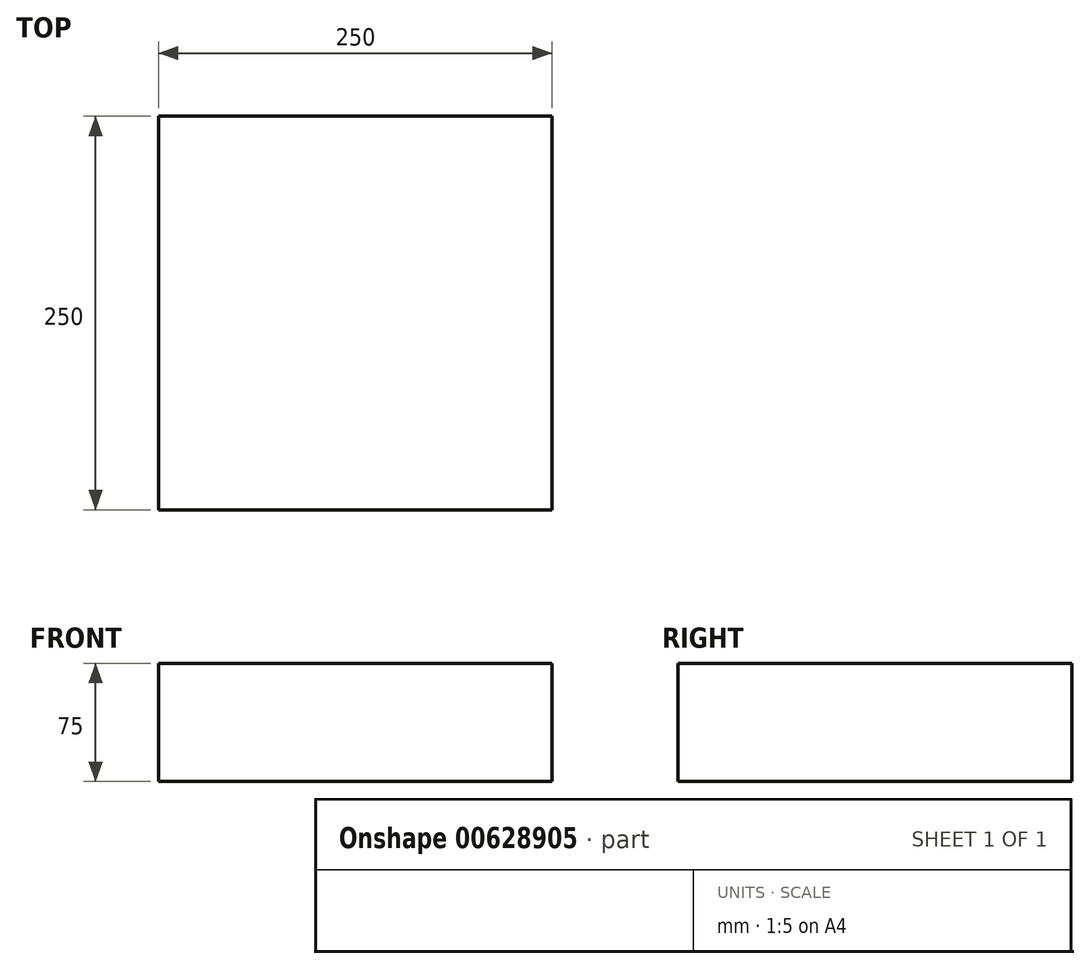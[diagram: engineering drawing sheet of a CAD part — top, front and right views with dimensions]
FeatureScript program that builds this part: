
annotation { "Feature Type Name" : "Feature", "Feature Type Description" : "" }
export const myFeature = defineFeature(function(context is Context, id is Id, definition is map)
    precondition{}
    {
        {
            var Q0;
            Q0=qCreatedBy(makeId("Top.planeOp"),FACE);
            var sketch = newSketch(context, id + "F0", { "sketchPlane" : qUnion([Q0])});
            skPoint(sketch, "E0.middle", {"position": v(0, 0) * mm});
            skLineSegment(sketch, "E1.bottom", {"start": v(125, -125) * mm, "end": v(-125, -125) * mm});
            skLineSegment(sketch, "E1.top", {"start": v(125, 125) * mm, "end": v(-125, 125) * mm});
            skLineSegment(sketch, "E1.left", {"start": v(125, -125) * mm, "end": v(125, 125) * mm});
            skLineSegment(sketch, "E1.right", {"start": v(-125, -125) * mm, "end": v(-125, 125) * mm});
            skSolve(sketch);
        }
        {
            var Q0;
            Q0=makeQuery(id+"F0.imprint","IMPRINT",FACE,{"disambiguationData":[TD([[makeQuery(id+"F0.imprint","IMPRINT",EDGE,{"derivedFrom":sQuery(id+"F0.wireOp",EDGE,"E1.bottom")}),-1.0]])]});
            extrude(context, id + "F1", {"entities" : qUnion([Q0]), "depth" : 5 * mm, "offsetDistance" : 25 * mm});
        }
        {
            var Q0;
            Q0=makeQuery(id+"F1.opExtrude","CAP_FACE",FACE,{"disambiguationData":[OSD([sQuery(id+"F0.wireOp",EDGE,"E1.bottom"),sQuery(id+"F0.wireOp",EDGE,"E1.top"),sQuery(id+"F0.wireOp",EDGE,"E1.left"),sQuery(id+"F0.wireOp",EDGE,"E1.right")])],"isStart":false});
            var sketch = newSketch(context, id + "F2", { "sketchPlane" : qUnion([Q0])});
            skLineSegment(sketch, "E2", {"start": v(-105, 115) * mm, "end": v(-105, -125) * mm});
            skLineSegment(sketch, "E3", {"start": v(-105, 115) * mm, "end": v(105, 115) * mm});
            skLineSegment(sketch, "E4", {"start": v(105, 115) * mm, "end": v(105, -125) * mm});
            skLineSegment(sketch, "E5", {"start": v(-105, -125) * mm, "end": v(-125, -125) * mm});
            skLineSegment(sketch, "E6", {"start": v(-125, -125) * mm, "end": v(-125, 125) * mm});
            skLineSegment(sketch, "E7", {"start": v(-125, 125) * mm, "end": v(125, 125) * mm});
            skLineSegment(sketch, "E8", {"start": v(125, 125) * mm, "end": v(125, -125) * mm});
            skLineSegment(sketch, "E9", {"start": v(125, -125) * mm, "end": v(105, -125) * mm});
            skSolve(sketch);
        }
        {
            var Q0;
            Q0=makeQuery(id+"F2.imprint","IMPRINT",FACE,{"disambiguationData":[TD([[makeQuery(id+"F2.imprint","IMPRINT",EDGE,{"derivedFrom":sQuery(id+"F2.wireOp",EDGE,"E2")}),-1.0]])]});
            extrude(context, id + "F3", {"entities" : qUnion([Q0]), "operationType" : NewBodyOperationType.ADD, "depth" : 70 * mm, "offsetDistance" : 25 * mm});
        }
        {
            var Q0;
            Q0=makeQuery(id+"F1.opExtrude","CAP_FACE",FACE,{"disambiguationData":[OSD([sQuery(id+"F0.wireOp",EDGE,"E1.bottom"),sQuery(id+"F0.wireOp",EDGE,"E1.top"),sQuery(id+"F0.wireOp",EDGE,"E1.left"),sQuery(id+"F0.wireOp",EDGE,"E1.right")])],"isStart":false});
            extrude(context, id + "F4", {"entities" : qUnion([Q0]), "operationType" : NewBodyOperationType.ADD, "depth" : 30 * mm, "offsetDistance" : 25 * mm});
        }
        {
            var Q0;
            Q0=makeQuery(id+"F4.opExtrude","CAP_FACE",FACE,{"disambiguationData":[OSD([sQuery(id+"F0.wireOp",EDGE,"E1.bottom"),sQuery(id+"F0.wireOp",EDGE,"E1.top"),sQuery(id+"F0.wireOp",EDGE,"E1.left"),sQuery(id+"F0.wireOp",EDGE,"E1.right")])],"isStart":false});
            var sketch = newSketch(context, id + "F5", { "sketchPlane" : qUnion([Q0])});
            skLineSegment(sketch, "E10", {"start": v(-105, 115) * mm, "end": v(-105, 85) * mm});
            skLineSegment(sketch, "E11", {"start": v(-105, 85) * mm, "end": v(-75, 85) * mm});
            skLineSegment(sketch, "E12", {"start": v(-75, 85) * mm, "end": v(-75, 115) * mm});
            skLineSegment(sketch, "E13", {"start": v(-75, 115) * mm, "end": v(-105, 115) * mm});
            skLineSegment(sketch, "E14.bottom", {"start": v(-75, 115) * mm, "end": v(-45, 115) * mm});
            skLineSegment(sketch, "E14.top", {"start": v(-75, 85) * mm, "end": v(-45, 85) * mm});
            skLineSegment(sketch, "E14.left", {"start": v(-75, 115) * mm, "end": v(-75, 85) * mm});
            skLineSegment(sketch, "E14.right", {"start": v(-45, 115) * mm, "end": v(-45, 85) * mm});
            skLineSegment(sketch, "E15.bottom", {"start": v(-45, 115) * mm, "end": v(-15, 115) * mm});
            skLineSegment(sketch, "E15.top", {"start": v(-45, 85) * mm, "end": v(-15, 85) * mm});
            skLineSegment(sketch, "E15.right", {"start": v(-15, 115) * mm, "end": v(-15, 85) * mm});
            skLineSegment(sketch, "E16.bottom", {"start": v(-15, 115) * mm, "end": v(15, 115) * mm});
            skLineSegment(sketch, "E16.top", {"start": v(-15, 85) * mm, "end": v(15, 85) * mm});
            skLineSegment(sketch, "E16.right", {"start": v(15, 115) * mm, "end": v(15, 85) * mm});
            skLineSegment(sketch, "E17.bottom", {"start": v(15, 115) * mm, "end": v(45, 115) * mm});
            skLineSegment(sketch, "E17.top", {"start": v(15, 85) * mm, "end": v(45, 85) * mm});
            skLineSegment(sketch, "E17.right", {"start": v(45, 115) * mm, "end": v(45, 85) * mm});
            skLineSegment(sketch, "E18.bottom", {"start": v(45, 115) * mm, "end": v(75, 115) * mm});
            skLineSegment(sketch, "E18.top", {"start": v(45, 85) * mm, "end": v(75, 85) * mm});
            skLineSegment(sketch, "E18.right", {"start": v(75, 115) * mm, "end": v(75, 85) * mm});
            skLineSegment(sketch, "E19.bottom", {"start": v(75, 115) * mm, "end": v(105, 115) * mm});
            skLineSegment(sketch, "E19.top", {"start": v(75, 85) * mm, "end": v(105, 85) * mm});
            skLineSegment(sketch, "E19.right", {"start": v(105, 115) * mm, "end": v(105, 85) * mm});
            skLineSegment(sketch, "E20.top", {"start": v(-105, 55) * mm, "end": v(-75, 55) * mm});
            skLineSegment(sketch, "E20.left", {"start": v(-105, 85) * mm, "end": v(-105, 55) * mm});
            skLineSegment(sketch, "E20.right", {"start": v(-75, 85) * mm, "end": v(-75, 55) * mm});
            skLineSegment(sketch, "E21.top", {"start": v(-105, 25) * mm, "end": v(-75, 25) * mm});
            skLineSegment(sketch, "E21.left", {"start": v(-105, 55) * mm, "end": v(-105, 25) * mm});
            skLineSegment(sketch, "E21.right", {"start": v(-75, 55) * mm, "end": v(-75, 25) * mm});
            skLineSegment(sketch, "E22.top", {"start": v(-105, -5) * mm, "end": v(-75, -5) * mm});
            skLineSegment(sketch, "E22.left", {"start": v(-105, 25) * mm, "end": v(-105, -5) * mm});
            skLineSegment(sketch, "E22.right", {"start": v(-75, 25) * mm, "end": v(-75, -5) * mm});
            skLineSegment(sketch, "E23.top", {"start": v(-105, -35) * mm, "end": v(-75, -35) * mm});
            skLineSegment(sketch, "E23.left", {"start": v(-105, -5) * mm, "end": v(-105, -35) * mm});
            skLineSegment(sketch, "E23.right", {"start": v(-75, -5) * mm, "end": v(-75, -35) * mm});
            skLineSegment(sketch, "E24.top", {"start": v(-105, -65) * mm, "end": v(-75, -65) * mm});
            skLineSegment(sketch, "E24.left", {"start": v(-105, -35) * mm, "end": v(-105, -65) * mm});
            skLineSegment(sketch, "E24.right", {"start": v(-75, -35) * mm, "end": v(-75, -65) * mm});
            skLineSegment(sketch, "E25.top", {"start": v(-105, -95) * mm, "end": v(-75, -95) * mm});
            skLineSegment(sketch, "E25.left", {"start": v(-105, -65) * mm, "end": v(-105, -95) * mm});
            skLineSegment(sketch, "E25.right", {"start": v(-75, -65) * mm, "end": v(-75, -95) * mm});
            skLineSegment(sketch, "E26.top", {"start": v(-105, -125) * mm, "end": v(-75, -125) * mm});
            skLineSegment(sketch, "E26.left", {"start": v(-105, -95) * mm, "end": v(-105, -125) * mm});
            skLineSegment(sketch, "E26.right", {"start": v(-75, -95) * mm, "end": v(-75, -125) * mm});
            skLineSegment(sketch, "E27.top", {"start": v(-75, 55) * mm, "end": v(-45, 55) * mm});
            skLineSegment(sketch, "E27.right", {"start": v(-45, 85) * mm, "end": v(-45, 55) * mm});
            skLineSegment(sketch, "E28.top", {"start": v(-45, 55) * mm, "end": v(-15, 55) * mm});
            skLineSegment(sketch, "E28.right", {"start": v(-15, 85) * mm, "end": v(-15, 55) * mm});
            skLineSegment(sketch, "E29.top", {"start": v(-15, 55) * mm, "end": v(15, 55) * mm});
            skLineSegment(sketch, "E29.right", {"start": v(15, 85) * mm, "end": v(15, 55) * mm});
            skLineSegment(sketch, "E30.top", {"start": v(15, 55) * mm, "end": v(45, 55) * mm});
            skLineSegment(sketch, "E30.right", {"start": v(45, 85) * mm, "end": v(45, 55) * mm});
            skLineSegment(sketch, "E31.top", {"start": v(45, 55) * mm, "end": v(75, 55) * mm});
            skLineSegment(sketch, "E31.right", {"start": v(75, 85) * mm, "end": v(75, 55) * mm});
            skLineSegment(sketch, "E32.top", {"start": v(75, 55) * mm, "end": v(105, 55) * mm});
            skLineSegment(sketch, "E32.right", {"start": v(105, 85) * mm, "end": v(105, 55) * mm});
            skLineSegment(sketch, "E33.top", {"start": v(-75, 25) * mm, "end": v(-45, 25) * mm});
            skLineSegment(sketch, "E33.right", {"start": v(-45, 55) * mm, "end": v(-45, 25) * mm});
            skLineSegment(sketch, "E34.top", {"start": v(-45, 25) * mm, "end": v(-15, 25) * mm});
            skLineSegment(sketch, "E34.right", {"start": v(-15, 55) * mm, "end": v(-15, 25) * mm});
            skLineSegment(sketch, "E35.top", {"start": v(-15, 25) * mm, "end": v(15, 25) * mm});
            skLineSegment(sketch, "E35.right", {"start": v(15, 55) * mm, "end": v(15, 25) * mm});
            skLineSegment(sketch, "E36.top", {"start": v(15, 25) * mm, "end": v(45, 25) * mm});
            skLineSegment(sketch, "E36.right", {"start": v(45, 55) * mm, "end": v(45, 25) * mm});
            skLineSegment(sketch, "E37.top", {"start": v(45, 25) * mm, "end": v(75, 25) * mm});
            skLineSegment(sketch, "E37.right", {"start": v(75, 55) * mm, "end": v(75, 25) * mm});
            skPoint(sketch, "E38.oppositeSnap0", {"position": v(105, 70) * mm});
            skLineSegment(sketch, "E38.top", {"start": v(75, 25) * mm, "end": v(105, 25) * mm});
            skLineSegment(sketch, "E38.right", {"start": v(105, 55) * mm, "end": v(105, 25) * mm});
            skLineSegment(sketch, "E39.top", {"start": v(-75, -5) * mm, "end": v(-45, -5) * mm});
            skLineSegment(sketch, "E39.right", {"start": v(-45, 25) * mm, "end": v(-45, -5) * mm});
            skLineSegment(sketch, "E40.top", {"start": v(-45, -5) * mm, "end": v(-15, -5) * mm});
            skLineSegment(sketch, "E40.right", {"start": v(-15, 25) * mm, "end": v(-15, -5) * mm});
            skLineSegment(sketch, "E41.top", {"start": v(-15, -5) * mm, "end": v(15, -5) * mm});
            skLineSegment(sketch, "E41.right", {"start": v(15, 25) * mm, "end": v(15, -5) * mm});
            skLineSegment(sketch, "E42.top", {"start": v(15, -5) * mm, "end": v(45, -5) * mm});
            skLineSegment(sketch, "E42.right", {"start": v(45, 25) * mm, "end": v(45, -5) * mm});
            skLineSegment(sketch, "E43.top", {"start": v(45, -5) * mm, "end": v(75, -5) * mm});
            skLineSegment(sketch, "E43.right", {"start": v(75, 25) * mm, "end": v(75, -5) * mm});
            skLineSegment(sketch, "E44.top", {"start": v(75, -5) * mm, "end": v(105, -5) * mm});
            skLineSegment(sketch, "E44.right", {"start": v(105, 25) * mm, "end": v(105, -5) * mm});
            skLineSegment(sketch, "E45.top", {"start": v(-75, -35) * mm, "end": v(-45, -35) * mm});
            skLineSegment(sketch, "E45.right", {"start": v(-45, -5) * mm, "end": v(-45, -35) * mm});
            skLineSegment(sketch, "E46.top", {"start": v(-45, -35) * mm, "end": v(-15, -35) * mm});
            skLineSegment(sketch, "E46.right", {"start": v(-15, -5) * mm, "end": v(-15, -35) * mm});
            skLineSegment(sketch, "E47.top", {"start": v(-15, -35) * mm, "end": v(15, -35) * mm});
            skLineSegment(sketch, "E47.right", {"start": v(15, -5) * mm, "end": v(15, -35) * mm});
            skLineSegment(sketch, "E48.top", {"start": v(15, -35) * mm, "end": v(45, -35) * mm});
            skLineSegment(sketch, "E48.right", {"start": v(45, -5) * mm, "end": v(45, -35) * mm});
            skLineSegment(sketch, "E49.top", {"start": v(45, -35) * mm, "end": v(75, -35) * mm});
            skLineSegment(sketch, "E49.right", {"start": v(75, -5) * mm, "end": v(75, -35) * mm});
            skLineSegment(sketch, "E50.top", {"start": v(75, -35) * mm, "end": v(105, -35) * mm});
            skLineSegment(sketch, "E50.right", {"start": v(105, -5) * mm, "end": v(105, -35) * mm});
            skLineSegment(sketch, "E51.top", {"start": v(-75, -65) * mm, "end": v(-45, -65) * mm});
            skLineSegment(sketch, "E51.right", {"start": v(-45, -35) * mm, "end": v(-45, -65) * mm});
            skLineSegment(sketch, "E52.top", {"start": v(-75, -95) * mm, "end": v(-45, -95) * mm});
            skLineSegment(sketch, "E52.right", {"start": v(-45, -65) * mm, "end": v(-45, -95) * mm});
            skLineSegment(sketch, "E53.top", {"start": v(-75, -125) * mm, "end": v(-45, -125) * mm});
            skLineSegment(sketch, "E53.right", {"start": v(-45, -95) * mm, "end": v(-45, -125) * mm});
            skPoint(sketch, "E54.oppositeSnap0", {"position": v(-15, 70) * mm});
            skLineSegment(sketch, "E54.top", {"start": v(-45, -65) * mm, "end": v(-15, -65) * mm});
            skLineSegment(sketch, "E54.right", {"start": v(-15, -35) * mm, "end": v(-15, -65) * mm});
            skLineSegment(sketch, "E55.top", {"start": v(-15, -65) * mm, "end": v(15, -65) * mm});
            skLineSegment(sketch, "E55.right", {"start": v(15, -35) * mm, "end": v(15, -65) * mm});
            skLineSegment(sketch, "E56.top", {"start": v(15, -65) * mm, "end": v(45, -65) * mm});
            skLineSegment(sketch, "E56.right", {"start": v(45, -35) * mm, "end": v(45, -65) * mm});
            skLineSegment(sketch, "E57.top", {"start": v(45, -65) * mm, "end": v(75, -65) * mm});
            skLineSegment(sketch, "E57.right", {"start": v(75, -35) * mm, "end": v(75, -65) * mm});
            skLineSegment(sketch, "E58.top", {"start": v(75, -65) * mm, "end": v(105, -65) * mm});
            skLineSegment(sketch, "E58.right", {"start": v(105, -35) * mm, "end": v(105, -65) * mm});
            skLineSegment(sketch, "E59.top", {"start": v(-45, -95) * mm, "end": v(-15, -95) * mm});
            skLineSegment(sketch, "E59.right", {"start": v(-15, -65) * mm, "end": v(-15, -95) * mm});
            skLineSegment(sketch, "E60.top", {"start": v(-15, -95) * mm, "end": v(15, -95) * mm});
            skLineSegment(sketch, "E60.right", {"start": v(15, -65) * mm, "end": v(15, -95) * mm});
            skLineSegment(sketch, "E61.top", {"start": v(-45, -125) * mm, "end": v(-15, -125) * mm});
            skLineSegment(sketch, "E61.right", {"start": v(-15, -95) * mm, "end": v(-15, -125) * mm});
            skLineSegment(sketch, "E62.top", {"start": v(-15, -125) * mm, "end": v(15, -125) * mm});
            skLineSegment(sketch, "E62.right", {"start": v(15, -95) * mm, "end": v(15, -125) * mm});
            skLineSegment(sketch, "E63.top", {"start": v(15, -95) * mm, "end": v(45, -95) * mm});
            skLineSegment(sketch, "E63.right", {"start": v(45, -65) * mm, "end": v(45, -95) * mm});
            skLineSegment(sketch, "E64.top", {"start": v(15, -125) * mm, "end": v(45, -125) * mm});
            skLineSegment(sketch, "E64.right", {"start": v(45, -95) * mm, "end": v(45, -125) * mm});
            skLineSegment(sketch, "E65.top", {"start": v(45, -95) * mm, "end": v(75, -95) * mm});
            skLineSegment(sketch, "E65.right", {"start": v(75, -65) * mm, "end": v(75, -95) * mm});
            skLineSegment(sketch, "E66.top", {"start": v(45, -125) * mm, "end": v(75, -125) * mm});
            skLineSegment(sketch, "E66.right", {"start": v(75, -95) * mm, "end": v(75, -125) * mm});
            skLineSegment(sketch, "E67.top", {"start": v(75, -95) * mm, "end": v(105, -95) * mm});
            skLineSegment(sketch, "E67.right", {"start": v(105, -65) * mm, "end": v(105, -95) * mm});
            skLineSegment(sketch, "E68.top", {"start": v(75, -125) * mm, "end": v(105, -125) * mm});
            skLineSegment(sketch, "E68.right", {"start": v(105, -95) * mm, "end": v(105, -125) * mm});
            skSolve(sketch);
        }
        {
            var Q0;
            Q0=makeQuery(id+"F5.imprint","IMPRINT",FACE,{"disambiguationData":[TD([[makeQuery(id+"F5.imprint","IMPRINT",EDGE,{"derivedFrom":sQuery(id+"F5.wireOp",EDGE,"E10")}),1.0]])]});
            var Q1;
            Q1=makeQuery(id+"F5.imprint","IMPRINT",FACE,{"disambiguationData":[TD([[makeQuery(id+"F5.imprint","IMPRINT",EDGE,{"derivedFrom":sQuery(id+"F5.wireOp",EDGE,"E14.top")}),-1.0]])]});
            var Q2;
            Q2=makeQuery(id+"F5.imprint","IMPRINT",FACE,{"disambiguationData":[TD([[makeQuery(id+"F5.imprint","IMPRINT",EDGE,{"derivedFrom":sQuery(id+"F5.wireOp",EDGE,"E14.bottom")}),-1.0]])]});
            var Q3;
            Q3=makeQuery(id+"F5.imprint","IMPRINT",FACE,{"disambiguationData":[TD([[makeQuery(id+"F5.imprint","IMPRINT",EDGE,{"derivedFrom":sQuery(id+"F5.wireOp",EDGE,"E11")}),-1.0]])]});
            var Q4;
            Q4=makeQuery(id+"F5.imprint","IMPRINT",FACE,{"disambiguationData":[TD([[makeQuery(id+"F5.imprint","IMPRINT",EDGE,{"derivedFrom":sQuery(id+"F5.wireOp",EDGE,"E20.top")}),-1.0]])]});
            var Q5;
            Q5=makeQuery(id+"F5.imprint","IMPRINT",FACE,{"disambiguationData":[TD([[makeQuery(id+"F5.imprint","IMPRINT",EDGE,{"derivedFrom":sQuery(id+"F5.wireOp",EDGE,"E21.top")}),-1.0]])]});
            var Q6;
            Q6=makeQuery(id+"F5.imprint","IMPRINT",FACE,{"disambiguationData":[TD([[makeQuery(id+"F5.imprint","IMPRINT",EDGE,{"derivedFrom":sQuery(id+"F5.wireOp",EDGE,"E22.top")}),-1.0]])]});
            var Q7;
            Q7=makeQuery(id+"F5.imprint","IMPRINT",FACE,{"disambiguationData":[TD([[makeQuery(id+"F5.imprint","IMPRINT",EDGE,{"derivedFrom":sQuery(id+"F5.wireOp",EDGE,"E23.top")}),-1.0]])]});
            var Q8;
            Q8=makeQuery(id+"F5.imprint","IMPRINT",FACE,{"disambiguationData":[TD([[makeQuery(id+"F5.imprint","IMPRINT",EDGE,{"derivedFrom":sQuery(id+"F5.wireOp",EDGE,"E24.top")}),-1.0]])]});
            var Q9;
            Q9=makeQuery(id+"F5.imprint","IMPRINT",FACE,{"disambiguationData":[TD([[makeQuery(id+"F5.imprint","IMPRINT",EDGE,{"derivedFrom":sQuery(id+"F5.wireOp",EDGE,"E25.top")}),-1.0]])]});
            var Q10;
            Q10=makeQuery(id+"F5.imprint","IMPRINT",FACE,{"disambiguationData":[TD([[makeQuery(id+"F5.imprint","IMPRINT",EDGE,{"derivedFrom":sQuery(id+"F5.wireOp",EDGE,"E52.top")}),-1.0]])]});
            var Q11;
            Q11=makeQuery(id+"F5.imprint","IMPRINT",FACE,{"disambiguationData":[TD([[makeQuery(id+"F5.imprint","IMPRINT",EDGE,{"derivedFrom":sQuery(id+"F5.wireOp",EDGE,"E51.top")}),-1.0]])]});
            var Q12;
            Q12=makeQuery(id+"F5.imprint","IMPRINT",FACE,{"disambiguationData":[TD([[makeQuery(id+"F5.imprint","IMPRINT",EDGE,{"derivedFrom":sQuery(id+"F5.wireOp",EDGE,"E45.top")}),-1.0]])]});
            var Q13;
            Q13=makeQuery(id+"F5.imprint","IMPRINT",FACE,{"disambiguationData":[TD([[makeQuery(id+"F5.imprint","IMPRINT",EDGE,{"derivedFrom":sQuery(id+"F5.wireOp",EDGE,"E39.top")}),-1.0]])]});
            var Q14;
            Q14=makeQuery(id+"F5.imprint","IMPRINT",FACE,{"disambiguationData":[TD([[makeQuery(id+"F5.imprint","IMPRINT",EDGE,{"derivedFrom":sQuery(id+"F5.wireOp",EDGE,"E33.top")}),-1.0]])]});
            var Q15;
            Q15=makeQuery(id+"F5.imprint","IMPRINT",FACE,{"disambiguationData":[TD([[makeQuery(id+"F5.imprint","IMPRINT",EDGE,{"derivedFrom":sQuery(id+"F5.wireOp",EDGE,"E27.top")}),-1.0]])]});
            var Q16;
            Q16=makeQuery(id+"F5.imprint","IMPRINT",FACE,{"disambiguationData":[TD([[makeQuery(id+"F5.imprint","IMPRINT",EDGE,{"derivedFrom":sQuery(id+"F5.wireOp",EDGE,"E15.bottom")}),-1.0]])]});
            var Q17;
            Q17=makeQuery(id+"F5.imprint","IMPRINT",FACE,{"disambiguationData":[TD([[makeQuery(id+"F5.imprint","IMPRINT",EDGE,{"derivedFrom":sQuery(id+"F5.wireOp",EDGE,"E15.top")}),-1.0]])]});
            var Q18;
            Q18=makeQuery(id+"F5.imprint","IMPRINT",FACE,{"disambiguationData":[TD([[makeQuery(id+"F5.imprint","IMPRINT",EDGE,{"derivedFrom":sQuery(id+"F5.wireOp",EDGE,"E28.top")}),-1.0]])]});
            var Q19;
            Q19=makeQuery(id+"F5.imprint","IMPRINT",FACE,{"disambiguationData":[TD([[makeQuery(id+"F5.imprint","IMPRINT",EDGE,{"derivedFrom":sQuery(id+"F5.wireOp",EDGE,"E34.top")}),-1.0]])]});
            var Q20;
            Q20=makeQuery(id+"F5.imprint","IMPRINT",FACE,{"disambiguationData":[TD([[makeQuery(id+"F5.imprint","IMPRINT",EDGE,{"derivedFrom":sQuery(id+"F5.wireOp",EDGE,"E40.top")}),-1.0]])]});
            var Q21;
            Q21=makeQuery(id+"F5.imprint","IMPRINT",FACE,{"disambiguationData":[TD([[makeQuery(id+"F5.imprint","IMPRINT",EDGE,{"derivedFrom":sQuery(id+"F5.wireOp",EDGE,"E59.top")}),-1.0]])]});
            var Q22;
            Q22=makeQuery(id+"F5.imprint","IMPRINT",FACE,{"disambiguationData":[TD([[makeQuery(id+"F5.imprint","IMPRINT",EDGE,{"derivedFrom":sQuery(id+"F5.wireOp",EDGE,"E54.top")}),-1.0]])]});
            var Q23;
            Q23=makeQuery(id+"F5.imprint","IMPRINT",FACE,{"disambiguationData":[TD([[makeQuery(id+"F5.imprint","IMPRINT",EDGE,{"derivedFrom":sQuery(id+"F5.wireOp",EDGE,"E46.top")}),-1.0]])]});
            var Q24;
            Q24=makeQuery(id+"F5.imprint","IMPRINT",FACE,{"disambiguationData":[TD([[makeQuery(id+"F5.imprint","IMPRINT",EDGE,{"derivedFrom":sQuery(id+"F5.wireOp",EDGE,"E60.top")}),-1.0]])]});
            var Q25;
            Q25=makeQuery(id+"F5.imprint","IMPRINT",FACE,{"disambiguationData":[TD([[makeQuery(id+"F5.imprint","IMPRINT",EDGE,{"derivedFrom":sQuery(id+"F5.wireOp",EDGE,"E55.top")}),-1.0]])]});
            var Q26;
            Q26=makeQuery(id+"F5.imprint","IMPRINT",FACE,{"disambiguationData":[TD([[makeQuery(id+"F5.imprint","IMPRINT",EDGE,{"derivedFrom":sQuery(id+"F5.wireOp",EDGE,"E47.top")}),-1.0]])]});
            var Q27;
            Q27=makeQuery(id+"F5.imprint","IMPRINT",FACE,{"disambiguationData":[TD([[makeQuery(id+"F5.imprint","IMPRINT",EDGE,{"derivedFrom":sQuery(id+"F5.wireOp",EDGE,"E41.top")}),-1.0]])]});
            var Q28;
            Q28=makeQuery(id+"F5.imprint","IMPRINT",FACE,{"disambiguationData":[TD([[makeQuery(id+"F5.imprint","IMPRINT",EDGE,{"derivedFrom":sQuery(id+"F5.wireOp",EDGE,"E35.top")}),-1.0]])]});
            var Q29;
            Q29=makeQuery(id+"F5.imprint","IMPRINT",FACE,{"disambiguationData":[TD([[makeQuery(id+"F5.imprint","IMPRINT",EDGE,{"derivedFrom":sQuery(id+"F5.wireOp",EDGE,"E29.top")}),-1.0]])]});
            var Q30;
            Q30=makeQuery(id+"F5.imprint","IMPRINT",FACE,{"disambiguationData":[TD([[makeQuery(id+"F5.imprint","IMPRINT",EDGE,{"derivedFrom":sQuery(id+"F5.wireOp",EDGE,"E16.top")}),-1.0]])]});
            var Q31;
            Q31=makeQuery(id+"F5.imprint","IMPRINT",FACE,{"disambiguationData":[TD([[makeQuery(id+"F5.imprint","IMPRINT",EDGE,{"derivedFrom":sQuery(id+"F5.wireOp",EDGE,"E16.bottom")}),-1.0]])]});
            var Q32;
            Q32=makeQuery(id+"F5.imprint","IMPRINT",FACE,{"disambiguationData":[TD([[makeQuery(id+"F5.imprint","IMPRINT",EDGE,{"derivedFrom":sQuery(id+"F5.wireOp",EDGE,"E17.bottom")}),-1.0]])]});
            var Q33;
            Q33=makeQuery(id+"F5.imprint","IMPRINT",FACE,{"disambiguationData":[TD([[makeQuery(id+"F5.imprint","IMPRINT",EDGE,{"derivedFrom":sQuery(id+"F5.wireOp",EDGE,"E17.top")}),-1.0]])]});
            var Q34;
            Q34=makeQuery(id+"F5.imprint","IMPRINT",FACE,{"disambiguationData":[TD([[makeQuery(id+"F5.imprint","IMPRINT",EDGE,{"derivedFrom":sQuery(id+"F5.wireOp",EDGE,"E30.top")}),-1.0]])]});
            var Q35;
            Q35=makeQuery(id+"F5.imprint","IMPRINT",FACE,{"disambiguationData":[TD([[makeQuery(id+"F5.imprint","IMPRINT",EDGE,{"derivedFrom":sQuery(id+"F5.wireOp",EDGE,"E36.top")}),-1.0]])]});
            var Q36;
            Q36=makeQuery(id+"F5.imprint","IMPRINT",FACE,{"disambiguationData":[TD([[makeQuery(id+"F5.imprint","IMPRINT",EDGE,{"derivedFrom":sQuery(id+"F5.wireOp",EDGE,"E42.top")}),-1.0]])]});
            var Q37;
            Q37=makeQuery(id+"F5.imprint","IMPRINT",FACE,{"disambiguationData":[TD([[makeQuery(id+"F5.imprint","IMPRINT",EDGE,{"derivedFrom":sQuery(id+"F5.wireOp",EDGE,"E48.top")}),-1.0]])]});
            var Q38;
            Q38=makeQuery(id+"F5.imprint","IMPRINT",FACE,{"disambiguationData":[TD([[makeQuery(id+"F5.imprint","IMPRINT",EDGE,{"derivedFrom":sQuery(id+"F5.wireOp",EDGE,"E56.top")}),-1.0]])]});
            var Q39;
            Q39=makeQuery(id+"F5.imprint","IMPRINT",FACE,{"disambiguationData":[TD([[makeQuery(id+"F5.imprint","IMPRINT",EDGE,{"derivedFrom":sQuery(id+"F5.wireOp",EDGE,"E63.top")}),-1.0]])]});
            var Q40;
            Q40=makeQuery(id+"F5.imprint","IMPRINT",FACE,{"disambiguationData":[TD([[makeQuery(id+"F5.imprint","IMPRINT",EDGE,{"derivedFrom":sQuery(id+"F5.wireOp",EDGE,"E65.top")}),-1.0]])]});
            var Q41;
            Q41=makeQuery(id+"F5.imprint","IMPRINT",FACE,{"disambiguationData":[TD([[makeQuery(id+"F5.imprint","IMPRINT",EDGE,{"derivedFrom":sQuery(id+"F5.wireOp",EDGE,"E57.top")}),-1.0]])]});
            var Q42;
            Q42=makeQuery(id+"F5.imprint","IMPRINT",FACE,{"disambiguationData":[TD([[makeQuery(id+"F5.imprint","IMPRINT",EDGE,{"derivedFrom":sQuery(id+"F5.wireOp",EDGE,"E49.top")}),-1.0]])]});
            var Q43;
            Q43=makeQuery(id+"F5.imprint","IMPRINT",FACE,{"disambiguationData":[TD([[makeQuery(id+"F5.imprint","IMPRINT",EDGE,{"derivedFrom":sQuery(id+"F5.wireOp",EDGE,"E43.top")}),-1.0]])]});
            var Q44;
            Q44=makeQuery(id+"F5.imprint","IMPRINT",FACE,{"disambiguationData":[TD([[makeQuery(id+"F5.imprint","IMPRINT",EDGE,{"derivedFrom":sQuery(id+"F5.wireOp",EDGE,"E37.top")}),-1.0]])]});
            var Q45;
            Q45=makeQuery(id+"F5.imprint","IMPRINT",FACE,{"disambiguationData":[TD([[makeQuery(id+"F5.imprint","IMPRINT",EDGE,{"derivedFrom":sQuery(id+"F5.wireOp",EDGE,"E31.top")}),-1.0]])]});
            var Q46;
            Q46=makeQuery(id+"F5.imprint","IMPRINT",FACE,{"disambiguationData":[TD([[makeQuery(id+"F5.imprint","IMPRINT",EDGE,{"derivedFrom":sQuery(id+"F5.wireOp",EDGE,"E18.top")}),-1.0]])]});
            var Q47;
            Q47=makeQuery(id+"F5.imprint","IMPRINT",FACE,{"disambiguationData":[TD([[makeQuery(id+"F5.imprint","IMPRINT",EDGE,{"derivedFrom":sQuery(id+"F5.wireOp",EDGE,"E18.bottom")}),-1.0]])]});
            var Q48;
            Q48=makeQuery(id+"F5.imprint","IMPRINT",FACE,{"disambiguationData":[TD([[makeQuery(id+"F5.imprint","IMPRINT",EDGE,{"derivedFrom":sQuery(id+"F5.wireOp",EDGE,"E67.top")}),-1.0]])]});
            var Q49;
            Q49=makeQuery(id+"F5.imprint","IMPRINT",FACE,{"disambiguationData":[TD([[makeQuery(id+"F5.imprint","IMPRINT",EDGE,{"derivedFrom":sQuery(id+"F5.wireOp",EDGE,"E58.top")}),-1.0]])]});
            var Q50;
            Q50=makeQuery(id+"F5.imprint","IMPRINT",FACE,{"disambiguationData":[TD([[makeQuery(id+"F5.imprint","IMPRINT",EDGE,{"derivedFrom":sQuery(id+"F5.wireOp",EDGE,"E50.top")}),-1.0]])]});
            var Q51;
            Q51=makeQuery(id+"F5.imprint","IMPRINT",FACE,{"disambiguationData":[TD([[makeQuery(id+"F5.imprint","IMPRINT",EDGE,{"derivedFrom":sQuery(id+"F5.wireOp",EDGE,"E38.top")}),-1.0]])]});
            var Q52;
            Q52=makeQuery(id+"F5.imprint","IMPRINT",FACE,{"disambiguationData":[TD([[makeQuery(id+"F5.imprint","IMPRINT",EDGE,{"derivedFrom":sQuery(id+"F5.wireOp",EDGE,"E44.top")}),-1.0]])]});
            var Q53;
            Q53=makeQuery(id+"F5.imprint","IMPRINT",FACE,{"disambiguationData":[TD([[makeQuery(id+"F5.imprint","IMPRINT",EDGE,{"derivedFrom":sQuery(id+"F5.wireOp",EDGE,"E32.top")}),-1.0]])]});
            var Q54;
            Q54=makeQuery(id+"F5.imprint","IMPRINT",FACE,{"disambiguationData":[TD([[makeQuery(id+"F5.imprint","IMPRINT",EDGE,{"derivedFrom":sQuery(id+"F5.wireOp",EDGE,"E19.top")}),-1.0]])]});
            var Q55;
            Q55=makeQuery(id+"F5.imprint","IMPRINT",FACE,{"disambiguationData":[TD([[makeQuery(id+"F5.imprint","IMPRINT",EDGE,{"derivedFrom":sQuery(id+"F5.wireOp",EDGE,"E19.bottom")}),-1.0]])]});
            extrude(context, id + "F6", {"entities" : qUnion([Q0, Q1, Q2, Q3, Q4, Q5, Q6, Q7, Q8, Q9, Q10, Q11, Q12, Q13, Q14, Q15, Q16, Q17, Q18, Q19, Q20, Q21, Q22, Q23, Q24, Q25, Q26, Q27, Q28, Q29, Q30, Q31, Q32, Q33, Q34, Q35, Q36, Q37, Q38, Q39, Q40, Q41, Q42, Q43, Q44, Q45, Q46, Q47, Q48, Q49, Q50, Q51, Q52, Q53, Q54, Q55]), "operationType" : NewBodyOperationType.ADD, "depth" : 40 * mm, "offsetDistance" : 25 * mm});
        }
    });
